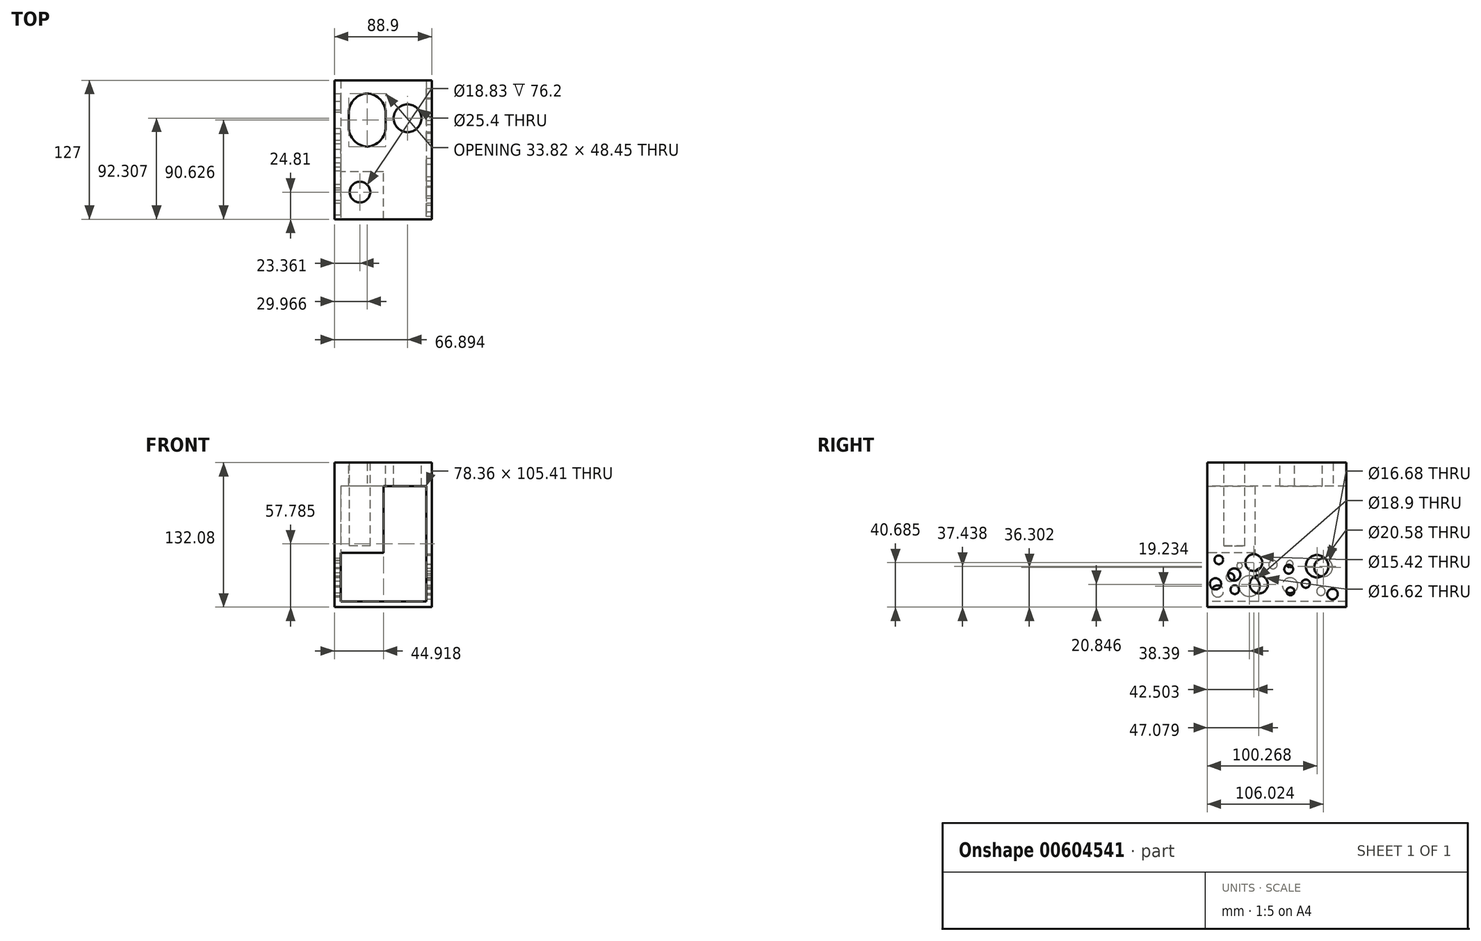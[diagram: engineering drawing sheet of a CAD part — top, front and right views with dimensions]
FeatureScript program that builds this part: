
annotation { "Feature Type Name" : "Feature", "Feature Type Description" : "" }
export const myFeature = defineFeature(function(context is Context, id is Id, definition is map)
    precondition{}
    {
        {
            var Q0;
            Q0=qCreatedBy(makeId("Top.planeOp"),FACE);
            var sketch = newSketch(context, id + "F0", { "sketchPlane" : qUnion([Q0])});
            skLineSegment(sketch, "E0.bottom", {"start": v(0, 0) * mm, "end": v(88.9, 0) * mm});
            skLineSegment(sketch, "E0.top", {"start": v(0, 127) * mm, "end": v(88.9, 127) * mm});
            skLineSegment(sketch, "E0.left", {"start": v(0, 0) * mm, "end": v(0, 127) * mm});
            skLineSegment(sketch, "E0.right", {"start": v(88.9, 0) * mm, "end": v(88.9, 127) * mm});
            skSolve(sketch);
        }
        {
            var Q0;
            Q0=makeQuery(id+"F0.imprint","IMPRINT",FACE,{"disambiguationData":[TD([[makeQuery(id+"F0.imprint","IMPRINT",EDGE,{"derivedFrom":sQuery(id+"F0.wireOp",EDGE,"E0.bottom")}),1.0]])]});
            extrude(context, id + "F1", {"entities" : qUnion([Q0]), "depth" : 88.9 * mm, "offsetDistance" : 25.4 * mm});
        }
        {
            var Q0;
            Q0=makeQuery(id+"F1.opExtrude","SWEPT_FACE",FACE,{"disambiguationData":[OSD([sQuery(id+"F0.wireOp",EDGE,"E0.bottom")])]});
            var sketch = newSketch(context, id + "F2", { "sketchPlane" : qUnion([Q0])});
            skPoint(sketch, "E1.oppositeSnap0", {"position": v(88.9, 44.45) * mm});
            skLineSegment(sketch, "E1.bottom", {"start": v(5.74, 0) * mm, "end": v(84.1, 0) * mm});
            skLineSegment(sketch, "E1.top", {"start": v(5.74, 44.45) * mm, "end": v(84.1, 44.45) * mm});
            skLineSegment(sketch, "E1.left", {"start": v(5.74, 0) * mm, "end": v(5.74, 44.45) * mm});
            skLineSegment(sketch, "E1.right", {"start": v(84.1, 0) * mm, "end": v(84.1, 44.45) * mm});
            skSolve(sketch);
        }
        {
            var Q0;
            Q0=makeQuery(id+"F1.opExtrude","CAP_FACE",FACE,{"disambiguationData":[OSD([sQuery(id+"F0.wireOp",EDGE,"E0.bottom"),sQuery(id+"F0.wireOp",EDGE,"E0.top"),sQuery(id+"F0.wireOp",EDGE,"E0.left"),sQuery(id+"F0.wireOp",EDGE,"E0.right")])],"isStart":true});
            extrude(context, id + "F3", {"entities" : qUnion([Q0]), "operationType" : NewBodyOperationType.ADD, "depth" : 5.08 * mm, "offsetDistance" : 25.4 * mm});
        }
        {
            var Q0;
            {var subQ0=sQuery(id+"F0.wireOp",EDGE,"E0.top");Q0=makeQuery(id+"F3.boolean.opBoolean","MERGE",FACE,{"derivedFrom":[makeQuery(id+"F1.opExtrude","SWEPT_FACE",FACE,{"disambiguationData":[OSD([subQ0])]}),makeQuery(id+"F3.opExtrude","SWEPT_FACE",FACE,{"disambiguationData":[OSD([subQ0])]})]});}
            extrude(context, id + "F4", {"entities" : qUnion([Q0]), "operationType" : NewBodyOperationType.ADD, "depth" : 25.4 * mm, "offsetDistance" : 25.4 * mm});
        }
        {
            var Q0;
            Q0=makeQuery(id+"F2.imprint","IMPRINT",FACE,{"disambiguationData":[TD([[makeQuery(id+"F2.imprint","IMPRINT",EDGE,{"derivedFrom":sQuery(id+"F2.wireOp",EDGE,"E1.bottom")}),1.0]])]});
            extrude(context, id + "F5", {"entities" : qUnion([Q0]), "operationType" : NewBodyOperationType.REMOVE, "oppositeDirection" : true, "depth" : 120.65 * mm, "offsetDistance" : 25.4 * mm});
        }
        {
            var Q0;
            Q0=makeQuery(id+"F4.opExtrude","CAP_FACE",FACE,{"disambiguationData":[OSD([sQuery(id+"F0.wireOp",EDGE,"E0.top")])],"isStart":false});
            extrude(context, id + "F6", {"entities" : qUnion([Q0]), "operationType" : NewBodyOperationType.REMOVE, "oppositeDirection" : true, "depth" : 25.4 * mm, "offsetDistance" : 25.4 * mm});
        }
        {
            var Q0;
            {var subQ0=sQuery(id+"F0.wireOp",EDGE,"E0.top");Q0=makeQuery(id+"F4.boolean.opBoolean","MERGE",FACE,{"derivedFrom":[makeQuery(id+"F1.opExtrude","CAP_FACE",FACE,{"disambiguationData":[OSD([sQuery(id+"F0.wireOp",EDGE,"E0.bottom"),subQ0,sQuery(id+"F0.wireOp",EDGE,"E0.left"),sQuery(id+"F0.wireOp",EDGE,"E0.right")])],"isStart":false}),makeQuery(id+"F4.opExtrude","SWEPT_FACE",FACE,{"disambiguationData":[OSD([subQ0]),TDD([makeQuery(id+"F1.opExtrude","CAP_EDGE",EDGE,{"disambiguationData":[OSD([subQ0])],"isStart":false})])]})]});}
            var sketch = newSketch(context, id + "F7", { "sketchPlane" : qUnion([Q0])});
            skCircle(sketch, "E2", {"center": v(23.36, 24.8) * mm, "radius": 9.42 * mm});
            skSolve(sketch);
        }
        {
            var Q0;
            Q0=makeQuery(id+"F7.imprint","IMPRINT",FACE,{"disambiguationData":[TD([[makeQuery(id+"F7.imprint","IMPRINT",EDGE,{"derivedFrom":sQuery(id+"F7.wireOp",EDGE,"E2")}),1.0]])]});
            extrude(context, id + "F8", {"entities" : qUnion([Q0]), "operationType" : NewBodyOperationType.REMOVE, "oppositeDirection" : true, "depth" : 38.1 * mm, "offsetDistance" : 25.4 * mm});
        }
        {
            var Q0;
            {var subQ0=sQuery(id+"F0.wireOp",EDGE,"E0.top");Q0=makeQuery(id+"F4.boolean.opBoolean","MERGE",FACE,{"derivedFrom":[makeQuery(id+"F1.opExtrude","CAP_FACE",FACE,{"disambiguationData":[OSD([sQuery(id+"F0.wireOp",EDGE,"E0.bottom"),subQ0,sQuery(id+"F0.wireOp",EDGE,"E0.left"),sQuery(id+"F0.wireOp",EDGE,"E0.right")])],"isStart":false}),makeQuery(id+"F4.opExtrude","SWEPT_FACE",FACE,{"disambiguationData":[OSD([subQ0]),TDD([makeQuery(id+"F1.opExtrude","CAP_EDGE",EDGE,{"disambiguationData":[OSD([subQ0])],"isStart":false})])]})]});}
            extrude(context, id + "F9", {"entities" : qUnion([Q0]), "operationType" : NewBodyOperationType.ADD, "depth" : 38.1 * mm, "offsetDistance" : 25.4 * mm});
        }
        {
            var Q0;
            Q0=makeQuery(id+"F5.boolean.opBoolean","COPY",FACE,{"derivedFrom":makeQuery(id+"F5.opExtrude","CAP_FACE",FACE,{"disambiguationData":[OSD([sQuery(id+"F2.wireOp",EDGE,"E1.bottom"),sQuery(id+"F2.wireOp",EDGE,"E1.top"),sQuery(id+"F2.wireOp",EDGE,"E1.left"),sQuery(id+"F2.wireOp",EDGE,"E1.right")])],"isStart":false})});
            extrude(context, id + "F10", {"entities" : qUnion([Q0]), "operationType" : NewBodyOperationType.ADD, "depth" : 25.4 * mm, "offsetDistance" : 25.4 * mm});
        }
        {
            var Q0;
            Q0=makeQuery(id+"F10.opExtrude","CAP_FACE",FACE,{"disambiguationData":[OSD([sQuery(id+"F2.wireOp",EDGE,"E1.bottom"),sQuery(id+"F2.wireOp",EDGE,"E1.top"),sQuery(id+"F2.wireOp",EDGE,"E1.left"),sQuery(id+"F2.wireOp",EDGE,"E1.right")])],"isStart":false});
            extrude(context, id + "F11", {"entities" : qUnion([Q0]), "operationType" : NewBodyOperationType.REMOVE, "oppositeDirection" : true, "depth" : 101.6 * mm, "offsetDistance" : 25.4 * mm});
        }
        {
            var Q0;
            {var subQ0=sQuery(id+"F0.wireOp",EDGE,"E0.left");var subQ1=sQuery(id+"F0.wireOp",EDGE,"E0.top");Q0=makeQuery(id+"F9.boolean.opBoolean","MERGE",FACE,{"derivedFrom":[makeQuery(id+"F4.boolean.opBoolean","MERGE",FACE,{"derivedFrom":[makeQuery(id+"F3.boolean.opBoolean","MERGE",FACE,{"derivedFrom":[makeQuery(id+"F1.opExtrude","SWEPT_FACE",FACE,{"disambiguationData":[OSD([subQ0])]}),makeQuery(id+"F3.opExtrude","SWEPT_FACE",FACE,{"disambiguationData":[OSD([subQ0])]})]}),makeQuery(id+"F4.opExtrude","SWEPT_FACE",FACE,{"disambiguationData":[OSD([subQ1,subQ0])]})]}),makeQuery(id+"F9.opExtrude","SWEPT_FACE",FACE,{"disambiguationData":[OSD([subQ1,subQ0])]})]});}
            var sketch = newSketch(context, id + "F12", { "sketchPlane" : qUnion([Q0])});
            skCircle(sketch, "E3", {"center": v(-20.9, 22.24) * mm, "radius": 3.78 * mm});
            skSolve(sketch);
        }
        {
            var Q0;
            Q0=makeQuery(id+"F12.imprint","IMPRINT",FACE,{"disambiguationData":[TD([[makeQuery(id+"F12.imprint","IMPRINT",EDGE,{"derivedFrom":sQuery(id+"F12.wireOp",EDGE,"E3")}),1.0]])]});
            extrude(context, id + "F13", {"entities" : qUnion([Q0]), "operationType" : NewBodyOperationType.REMOVE, "oppositeDirection" : true, "depth" : 25.4 * mm, "offsetDistance" : 25.4 * mm});
        }
        {
            var Q0;
            {var subQ0=sQuery(id+"F0.wireOp",EDGE,"E0.left");var subQ1=sQuery(id+"F0.wireOp",EDGE,"E0.top");Q0=makeQuery(id+"F9.boolean.opBoolean","MERGE",FACE,{"derivedFrom":[makeQuery(id+"F4.boolean.opBoolean","MERGE",FACE,{"derivedFrom":[makeQuery(id+"F3.boolean.opBoolean","MERGE",FACE,{"derivedFrom":[makeQuery(id+"F1.opExtrude","SWEPT_FACE",FACE,{"disambiguationData":[OSD([subQ0])]}),makeQuery(id+"F3.opExtrude","SWEPT_FACE",FACE,{"disambiguationData":[OSD([subQ0])]})]}),makeQuery(id+"F4.opExtrude","SWEPT_FACE",FACE,{"disambiguationData":[OSD([subQ1,subQ0])]})]}),makeQuery(id+"F9.opExtrude","SWEPT_FACE",FACE,{"disambiguationData":[OSD([subQ1,subQ0])]})]});}
            var sketch = newSketch(context, id + "F14", { "sketchPlane" : qUnion([Q0])});
            skCircle(sketch, "E4", {"center": v(-106.02, 31.22) * mm, "radius": 8.34 * mm});
            skSolve(sketch);
        }
        {
            var Q0;
            Q0=makeQuery(id+"F14.imprint","IMPRINT",FACE,{"disambiguationData":[TD([[makeQuery(id+"F14.imprint","IMPRINT",EDGE,{"derivedFrom":sQuery(id+"F14.wireOp",EDGE,"E4")}),1.0]])]});
            extrude(context, id + "F15", {"entities" : qUnion([Q0]), "operationType" : NewBodyOperationType.REMOVE, "oppositeDirection" : true, "depth" : 25.4 * mm, "offsetDistance" : 25.4 * mm});
        }
        {
            var Q0;
            {var subQ0=sQuery(id+"F0.wireOp",EDGE,"E0.left");var subQ1=sQuery(id+"F0.wireOp",EDGE,"E0.top");Q0=makeQuery(id+"F9.boolean.opBoolean","MERGE",FACE,{"derivedFrom":[makeQuery(id+"F4.boolean.opBoolean","MERGE",FACE,{"derivedFrom":[makeQuery(id+"F3.boolean.opBoolean","MERGE",FACE,{"derivedFrom":[makeQuery(id+"F1.opExtrude","SWEPT_FACE",FACE,{"disambiguationData":[OSD([subQ0])]}),makeQuery(id+"F3.opExtrude","SWEPT_FACE",FACE,{"disambiguationData":[OSD([subQ0])]})]}),makeQuery(id+"F4.opExtrude","SWEPT_FACE",FACE,{"disambiguationData":[OSD([subQ1,subQ0])]})]}),makeQuery(id+"F9.opExtrude","SWEPT_FACE",FACE,{"disambiguationData":[OSD([subQ1,subQ0])]})]});}
            var sketch = newSketch(context, id + "F16", { "sketchPlane" : qUnion([Q0])});
            skCircle(sketch, "E5", {"center": v(-75.64, 14.8) * mm, "radius": 7 * mm});
            skSolve(sketch);
        }
        {
            var Q0;
            Q0=makeQuery(id+"F16.imprint","IMPRINT",FACE,{"disambiguationData":[TD([[makeQuery(id+"F16.imprint","IMPRINT",EDGE,{"derivedFrom":sQuery(id+"F16.wireOp",EDGE,"E5")}),1.0]])]});
            extrude(context, id + "F17", {"entities" : qUnion([Q0]), "operationType" : NewBodyOperationType.REMOVE, "oppositeDirection" : true, "depth" : 25.4 * mm, "offsetDistance" : 25.4 * mm});
        }
        {
            var Q0;
            {var subQ0=sQuery(id+"F0.wireOp",EDGE,"E0.left");var subQ1=sQuery(id+"F0.wireOp",EDGE,"E0.top");Q0=makeQuery(id+"F9.boolean.opBoolean","MERGE",FACE,{"derivedFrom":[makeQuery(id+"F4.boolean.opBoolean","MERGE",FACE,{"derivedFrom":[makeQuery(id+"F3.boolean.opBoolean","MERGE",FACE,{"derivedFrom":[makeQuery(id+"F1.opExtrude","SWEPT_FACE",FACE,{"disambiguationData":[OSD([subQ0])]}),makeQuery(id+"F3.opExtrude","SWEPT_FACE",FACE,{"disambiguationData":[OSD([subQ0])]})]}),makeQuery(id+"F4.opExtrude","SWEPT_FACE",FACE,{"disambiguationData":[OSD([subQ1,subQ0])]})]}),makeQuery(id+"F9.opExtrude","SWEPT_FACE",FACE,{"disambiguationData":[OSD([subQ1,subQ0])]})]});}
            var sketch = newSketch(context, id + "F18", { "sketchPlane" : qUnion([Q0])});
            skCircle(sketch, "E6", {"center": v(-60, 33.84) * mm, "radius": 3.85 * mm});
            skSolve(sketch);
        }
        {
            var Q0;
            Q0=makeQuery(id+"F18.imprint","IMPRINT",FACE,{"disambiguationData":[TD([[makeQuery(id+"F18.imprint","IMPRINT",EDGE,{"derivedFrom":sQuery(id+"F18.wireOp",EDGE,"E6")}),1.0]])]});
            extrude(context, id + "F19", {"entities" : qUnion([Q0]), "operationType" : NewBodyOperationType.REMOVE, "oppositeDirection" : true, "depth" : 25.4 * mm, "offsetDistance" : 25.4 * mm});
        }
        {
            var Q0;
            {var subQ0=sQuery(id+"F2.wireOp",EDGE,"E1.left");Q0=makeQuery(id+"F11.boolean.opBoolean","MERGE",FACE,{"derivedFrom":[makeQuery(id+"F5.boolean.opBoolean","COPY",FACE,{"derivedFrom":makeQuery(id+"F5.opExtrude","SWEPT_FACE",FACE,{"disambiguationData":[OSD([subQ0])]})}),makeQuery(id+"F11.opExtrude","SWEPT_FACE",FACE,{"disambiguationData":[OSD([subQ0])]})]});}
            var sketch = newSketch(context, id + "F20", { "sketchPlane" : qUnion([Q0])});
            skCircle(sketch, "E7", {"center": v(38.4, 14.15) * mm, "radius": 9.45 * mm});
            skSolve(sketch);
        }
        {
            var Q0;
            Q0=makeQuery(id+"F20.imprint","IMPRINT",FACE,{"disambiguationData":[TD([[makeQuery(id+"F20.imprint","IMPRINT",EDGE,{"derivedFrom":sQuery(id+"F20.wireOp",EDGE,"E7")}),1.0]])]});
            extrude(context, id + "F21", {"entities" : qUnion([Q0]), "operationType" : NewBodyOperationType.REMOVE, "oppositeDirection" : true, "depth" : 25.4 * mm, "offsetDistance" : 25.4 * mm});
        }
        {
            var Q0;
            {var subQ0=sQuery(id+"F2.wireOp",EDGE,"E1.left");Q0=makeQuery(id+"F11.boolean.opBoolean","MERGE",FACE,{"derivedFrom":[makeQuery(id+"F5.boolean.opBoolean","COPY",FACE,{"derivedFrom":makeQuery(id+"F5.opExtrude","SWEPT_FACE",FACE,{"disambiguationData":[OSD([subQ0])]})}),makeQuery(id+"F11.opExtrude","SWEPT_FACE",FACE,{"disambiguationData":[OSD([subQ0])]})]});}
            var sketch = newSketch(context, id + "F22", { "sketchPlane" : qUnion([Q0])});
            skCircle(sketch, "E8", {"center": v(103.8, 9.5) * mm, "radius": 3.9 * mm});
            skCircle(sketch, "E9", {"center": v(29.46, 32.87) * mm, "radius": 2.5 * mm});
            skCircle(sketch, "E10", {"center": v(9.47, 9.5) * mm, "radius": 5.35 * mm});
            skCircle(sketch, "E11", {"center": v(47.96, 26.77) * mm, "radius": 3.59 * mm});
            skCircle(sketch, "E12", {"center": v(75.32, 34.48) * mm, "radius": 3.08 * mm});
            skSolve(sketch);
        }
        {
            var Q0;
            Q0 = qSketchRegion(id + "F22", true);
            extrude(context, id + "F23", {"entities" : qUnion([Q0]), "operationType" : NewBodyOperationType.REMOVE, "oppositeDirection" : true, "depth" : 25.4 * mm, "offsetDistance" : 25.4 * mm});
        }
        {
            var Q0;
            {var subQ0=sQuery(id+"F2.wireOp",EDGE,"E1.right");Q0=makeQuery(id+"F11.boolean.opBoolean","MERGE",FACE,{"derivedFrom":[makeQuery(id+"F5.boolean.opBoolean","COPY",FACE,{"derivedFrom":makeQuery(id+"F5.opExtrude","SWEPT_FACE",FACE,{"disambiguationData":[OSD([subQ0])]})}),makeQuery(id+"F11.opExtrude","SWEPT_FACE",FACE,{"disambiguationData":[OSD([subQ0])]})]});}
            var sketch = newSketch(context, id + "F24", { "sketchPlane" : qUnion([Q0])});
            skCircle(sketch, "E13", {"center": v(-100.27, 32.36) * mm, "radius": 10.29 * mm});
            skCircle(sketch, "E14", {"center": v(-89.94, 16.4) * mm, "radius": 3.76 * mm});
            skCircle(sketch, "E15", {"center": v(-114.42, 6.87) * mm, "radius": 4.82 * mm});
            skCircle(sketch, "E16", {"center": v(-42.5, 35.6) * mm, "radius": 7.7 * mm});
            skCircle(sketch, "E17", {"center": v(-74.37, 29.62) * mm, "radius": 4.07 * mm});
            skCircle(sketch, "E18", {"center": v(-47.08, 15.77) * mm, "radius": 8.31 * mm});
            skCircle(sketch, "E19", {"center": v(-7.51, 16.3) * mm, "radius": 5.13 * mm});
            skCircle(sketch, "E20", {"center": v(-24.6, 24.77) * mm, "radius": 5.56 * mm});
            skCircle(sketch, "E21", {"center": v(-10.52, 38.18) * mm, "radius": 3.95 * mm});
            skCircle(sketch, "E22", {"center": v(-75.92, 9.42) * mm, "radius": 3.63 * mm});
            skCircle(sketch, "E23", {"center": v(-25.11, 10.86) * mm, "radius": 3.93 * mm});
            skSolve(sketch);
        }
        {
            var Q0;
            Q0 = qSketchRegion(id + "F24", true);
            extrude(context, id + "F25", {"entities" : qUnion([Q0]), "operationType" : NewBodyOperationType.REMOVE, "oppositeDirection" : true, "depth" : 25.4 * mm, "offsetDistance" : 25.4 * mm});
        }
        {
            var Q0;
            {var subQ0=sQuery(id+"F2.wireOp",EDGE,"E1.top");Q0=makeQuery(id+"F11.boolean.opBoolean","MERGE",FACE,{"derivedFrom":[makeQuery(id+"F5.boolean.opBoolean","COPY",FACE,{"derivedFrom":makeQuery(id+"F5.opExtrude","SWEPT_FACE",FACE,{"disambiguationData":[OSD([subQ0])]})}),makeQuery(id+"F11.opExtrude","SWEPT_FACE",FACE,{"disambiguationData":[OSD([subQ0])]})]});}
            var sketch = newSketch(context, id + "F26", { "sketchPlane" : qUnion([Q0])});
            skLineSegment(sketch, "E24.bottom", {"start": v(44.92, 0) * mm, "end": v(5.74, 0) * mm});
            skLineSegment(sketch, "E24.top", {"start": v(44.92, -43.43) * mm, "end": v(5.74, -43.43) * mm});
            skLineSegment(sketch, "E24.left", {"start": v(44.92, 0) * mm, "end": v(44.92, -43.43) * mm});
            skLineSegment(sketch, "E24.right", {"start": v(5.74, 0) * mm, "end": v(5.74, -43.43) * mm});
            skSolve(sketch);
        }
        {
            var Q0;
            {var subQ5=sQuery(id+"F26.wireOp",EDGE,"E24.top");Q0=makeQuery(id+"F26.imprint","IMPRINT",FACE,{"disambiguationData":[TD([[makeQuery(id+"F26.imprint","IMPRINT",EDGE,{"derivedFrom":subQ5}),1.0]])]});}
            extrude(context, id + "F27", {"entities" : qUnion([Q0]), "operationType" : NewBodyOperationType.REMOVE, "oppositeDirection" : true, "depth" : 60.96 * mm, "offsetDistance" : 25.4 * mm});
        }
        {
            var Q0;
            Q0=makeQuery(id+"F9.opExtrude","CAP_FACE",FACE,{"disambiguationData":[OSD([sQuery(id+"F0.wireOp",EDGE,"E0.bottom"),sQuery(id+"F0.wireOp",EDGE,"E0.top"),sQuery(id+"F0.wireOp",EDGE,"E0.left"),sQuery(id+"F0.wireOp",EDGE,"E0.right")])],"isStart":false});
            var sketch = newSketch(context, id + "F28", { "sketchPlane" : qUnion([Q0])});
            skLineSegment(sketch, "E25.bottom", {"start": v(13.05, 114.87) * mm, "end": v(46.88, 114.87) * mm});
            skLineSegment(sketch, "E25.top", {"start": v(13.05, 66.38) * mm, "end": v(46.88, 66.38) * mm});
            skLineSegment(sketch, "E25.left", {"start": v(13.05, 114.87) * mm, "end": v(13.05, 66.38) * mm});
            skLineSegment(sketch, "E25.right", {"start": v(46.88, 114.87) * mm, "end": v(46.88, 66.38) * mm});
            skSolve(sketch);
        }
        {
            var Q0;
            Q0=makeQuery(id+"F28.imprint","IMPRINT",FACE,{"disambiguationData":[TD([[makeQuery(id+"F28.imprint","IMPRINT",EDGE,{"derivedFrom":sQuery(id+"F28.wireOp",EDGE,"E25.bottom")}),-1.0]])]});
            extrude(context, id + "F29", {"entities" : qUnion([Q0]), "operationType" : NewBodyOperationType.REMOVE, "oppositeDirection" : true, "depth" : 25.4 * mm, "offsetDistance" : 25.4 * mm});
        }
        {
            var Q0;
            Q0=makeQuery(id+"F29.boolean.opBoolean","COPY",EDGE,{"derivedFrom":makeQuery(id+"F29.opExtrude","SWEPT_EDGE",EDGE,{"disambiguationData":[OSD([sQuery(id+"F28.wireOp",EDGE,"E25.top"),sQuery(id+"F28.wireOp",EDGE,"E25.right")])]})});
            var Q1;
            Q1=makeQuery(id+"F29.boolean.opBoolean","COPY",EDGE,{"derivedFrom":makeQuery(id+"F29.opExtrude","SWEPT_EDGE",EDGE,{"disambiguationData":[OSD([sQuery(id+"F28.wireOp",EDGE,"E25.top"),sQuery(id+"F28.wireOp",EDGE,"E25.left")])]})});
            var Q2;
            Q2=makeQuery(id+"F29.boolean.opBoolean","COPY",EDGE,{"derivedFrom":makeQuery(id+"F29.opExtrude","SWEPT_EDGE",EDGE,{"disambiguationData":[OSD([sQuery(id+"F28.wireOp",EDGE,"E25.bottom"),sQuery(id+"F28.wireOp",EDGE,"E25.right")])]})});
            var Q3;
            Q3=makeQuery(id+"F29.boolean.opBoolean","COPY",EDGE,{"derivedFrom":makeQuery(id+"F29.opExtrude","SWEPT_EDGE",EDGE,{"disambiguationData":[OSD([sQuery(id+"F28.wireOp",EDGE,"E25.bottom"),sQuery(id+"F28.wireOp",EDGE,"E25.left")])]})});
            fillet(context, id + "F30", {"entities" : qUnion([Q0, Q1, Q2, Q3]), "radius" : 17.78 * mm, "tangentPropagation" : true, "allowEdgeOverflow" : false});
        }
        {
            var Q0;
            Q0=makeQuery(id+"F9.opExtrude","CAP_FACE",FACE,{"disambiguationData":[OSD([sQuery(id+"F0.wireOp",EDGE,"E0.bottom"),sQuery(id+"F0.wireOp",EDGE,"E0.top"),sQuery(id+"F0.wireOp",EDGE,"E0.left"),sQuery(id+"F0.wireOp",EDGE,"E0.right")])],"isStart":false});
            var sketch = newSketch(context, id + "F31", { "sketchPlane" : qUnion([Q0])});
            skCircle(sketch, "E26", {"center": v(66.9, 92.3) * mm, "radius": 12.7 * mm});
            skSolve(sketch);
        }
        {
            var Q0;
            Q0=makeQuery(id+"F31.imprint","IMPRINT",FACE,{"disambiguationData":[TD([[makeQuery(id+"F31.imprint","IMPRINT",EDGE,{"derivedFrom":sQuery(id+"F31.wireOp",EDGE,"E26")}),1.0]])]});
            extrude(context, id + "F32", {"entities" : qUnion([Q0]), "operationType" : NewBodyOperationType.REMOVE, "oppositeDirection" : true, "depth" : 25.4 * mm, "offsetDistance" : 25.4 * mm});
        }
    });
